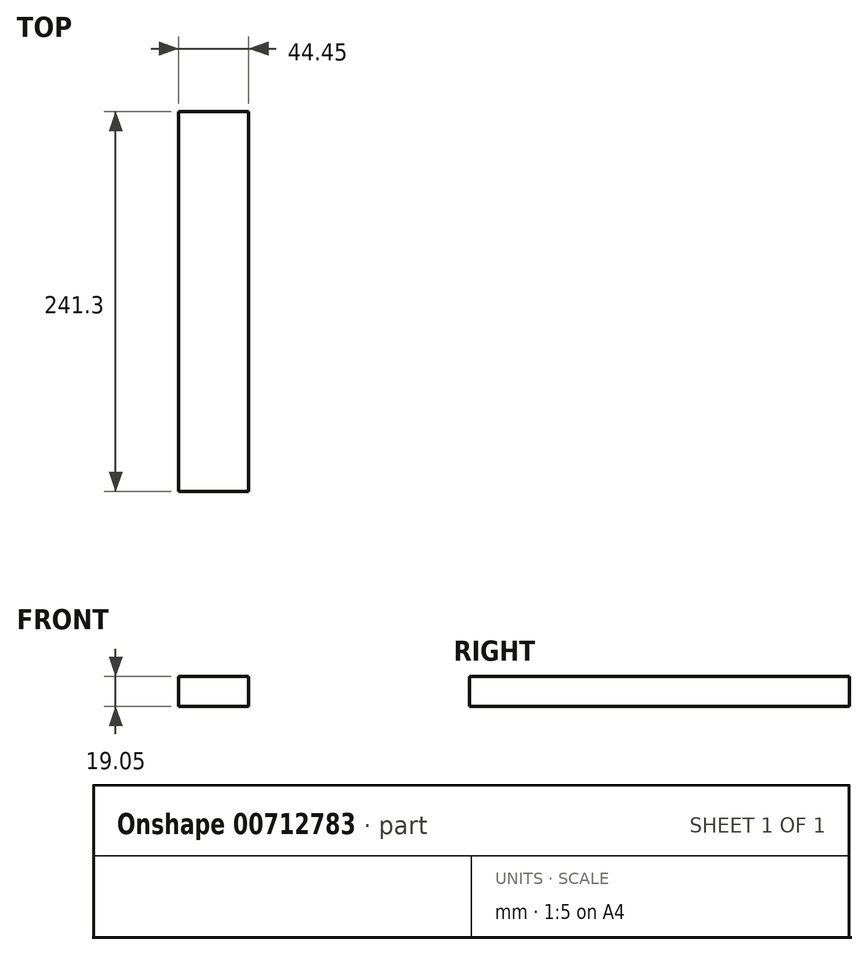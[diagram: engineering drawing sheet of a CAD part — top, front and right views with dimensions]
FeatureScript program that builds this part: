
annotation { "Feature Type Name" : "Feature", "Feature Type Description" : "" }
export const myFeature = defineFeature(function(context is Context, id is Id, definition is map)
    precondition{}
    {
        {
            var Q0;
            Q0=qCreatedBy(makeId("Front.planeOp"),FACE);
            var sketch = newSketch(context, id + "F0", { "sketchPlane" : qUnion([Q0])});
            skLineSegment(sketch, "E0.bottom", {"start": v(0, 0) * mm, "end": v(-44.45, 0) * mm});
            skLineSegment(sketch, "E0.top", {"start": v(0, 19.05) * mm, "end": v(-44.45, 19.05) * mm});
            skLineSegment(sketch, "E0.left", {"start": v(0, 0) * mm, "end": v(0, 19.05) * mm});
            skLineSegment(sketch, "E0.right", {"start": v(-44.45, 0) * mm, "end": v(-44.45, 19.05) * mm});
            skSolve(sketch);
        }
        {
            var Q0;
            Q0 = qSketchRegion(id + "F0", true);
            extrude(context, id + "F1", {"entities" : qUnion([Q0]), "depth" : 241.3 * mm, "offsetDistance" : 25.4 * mm});
        }
    });
